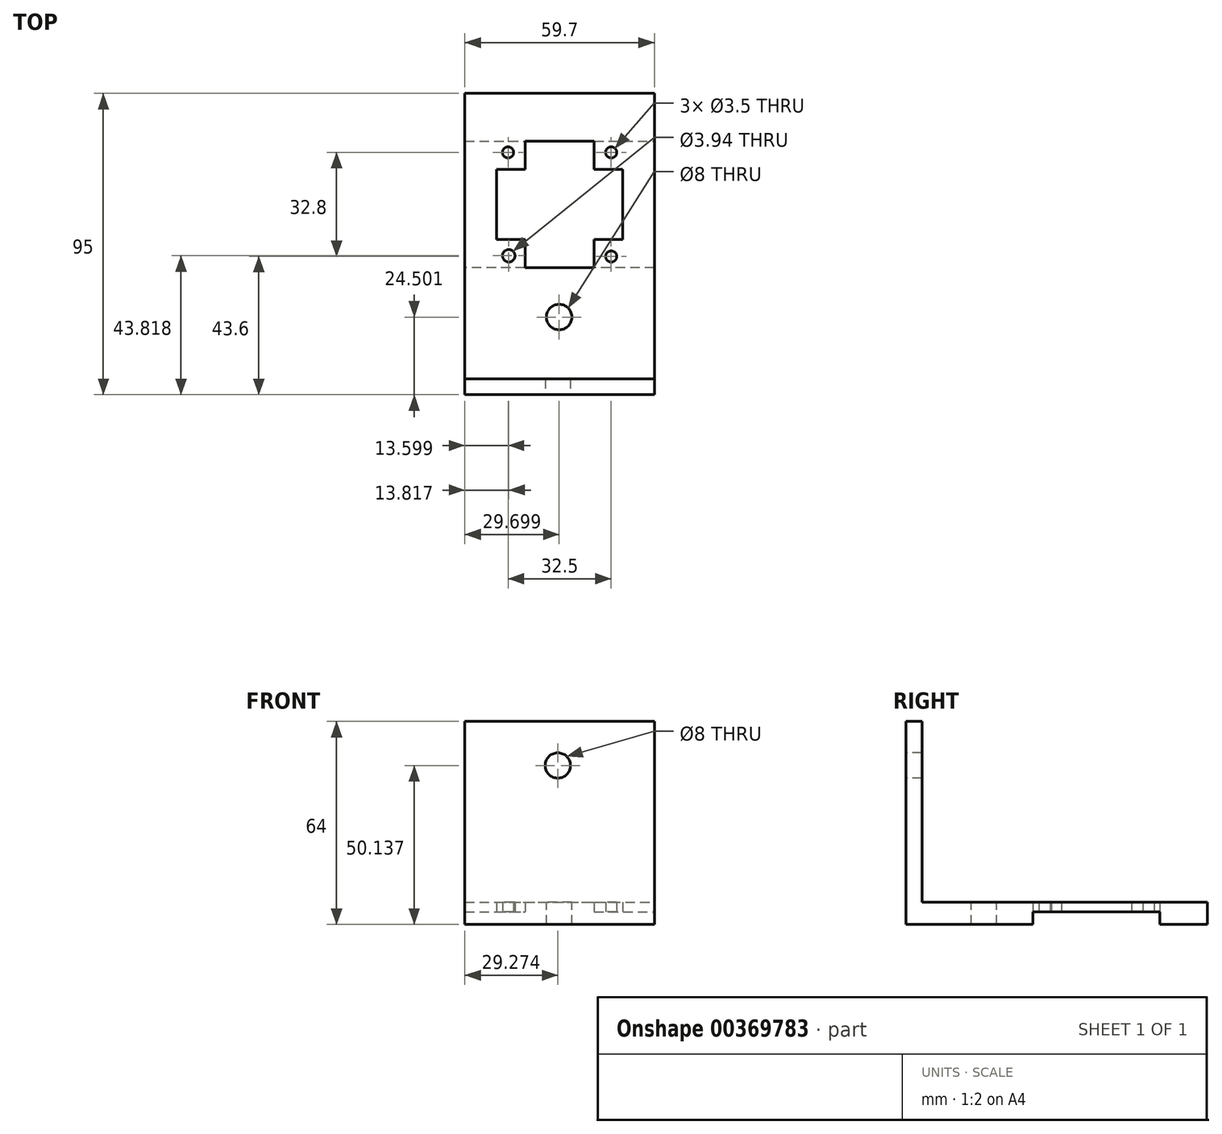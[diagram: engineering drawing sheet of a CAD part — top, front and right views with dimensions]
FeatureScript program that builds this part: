
annotation { "Feature Type Name" : "Feature", "Feature Type Description" : "" }
export const myFeature = defineFeature(function(context is Context, id is Id, definition is map)
    precondition{}
    {
        {
            var Q0;
            Q0=qCreatedBy(makeId("Top.planeOp"),FACE);
            var sketch = newSketch(context, id + "F0", { "sketchPlane" : qUnion([Q0])});
            skLineSegment(sketch, "E0.bottom", {"start": v(14.46, 0) * mm, "end": v(54.16, 0) * mm});
            skLineSegment(sketch, "E0.top", {"start": v(14.46, -40) * mm, "end": v(54.16, -40) * mm});
            skLineSegment(sketch, "E0.left", {"start": v(14.46, 0) * mm, "end": v(14.46, -40) * mm});
            skLineSegment(sketch, "E0.right", {"start": v(54.16, 0) * mm, "end": v(54.16, -40) * mm});
            skLineSegment(sketch, "E1", {"start": v(14.46, -9) * mm, "end": v(23.46, -9) * mm});
            skLineSegment(sketch, "E2", {"start": v(23.46, -9) * mm, "end": v(23.46, 0) * mm});
            skLineSegment(sketch, "E3", {"start": v(45.16, 0) * mm, "end": v(45.16, -9) * mm});
            skLineSegment(sketch, "E4", {"start": v(45.16, -9) * mm, "end": v(54.16, -9) * mm});
            skLineSegment(sketch, "E5", {"start": v(14.46, -31) * mm, "end": v(23.46, -31) * mm});
            skLineSegment(sketch, "E6", {"start": v(23.46, -31) * mm, "end": v(23.46, -40) * mm});
            skLineSegment(sketch, "E7", {"start": v(45.16, -40) * mm, "end": v(45.16, -31) * mm});
            skLineSegment(sketch, "E8", {"start": v(45.16, -31) * mm, "end": v(54.16, -31) * mm});
            skCircle(sketch, "E9", {"center": v(18.28, -36.18) * mm, "radius": 1.97 * mm});
            skCircle(sketch, "E10", {"center": v(18.06, -3.6) * mm, "radius": 1.75 * mm});
            skCircle(sketch, "E11", {"center": v(50.56, -3.6) * mm, "radius": 1.75 * mm});
            skCircle(sketch, "E12", {"center": v(50.56, -36.4) * mm, "radius": 1.75 * mm});
            skLineSegment(sketch, "E13", {"start": v(14.46, -40) * mm, "end": v(4.46, -40) * mm});
            skLineSegment(sketch, "E14", {"start": v(4.46, -40) * mm, "end": v(4.46, -50) * mm});
            skLineSegment(sketch, "E15", {"start": v(14.46, 0) * mm, "end": v(4.46, 0) * mm});
            skLineSegment(sketch, "E16", {"start": v(14.46, 0) * mm, "end": v(14.46, 10) * mm});
            skLineSegment(sketch, "E17", {"start": v(4.46, 0) * mm, "end": v(4.46, -40) * mm});
            skLineSegment(sketch, "E18", {"start": v(4.46, 0) * mm, "end": v(4.46, 10) * mm});
            skLineSegment(sketch, "E19", {"start": v(4.46, 10) * mm, "end": v(14.46, 10) * mm});
            skLineSegment(sketch, "E20", {"start": v(54.16, -40) * mm, "end": v(64.16, -40) * mm});
            skLineSegment(sketch, "E21", {"start": v(64.16, -40) * mm, "end": v(64.16, -50) * mm});
            skLineSegment(sketch, "E22", {"start": v(54.16, 0) * mm, "end": v(54.16, 10) * mm});
            skLineSegment(sketch, "E23", {"start": v(54.16, 0) * mm, "end": v(64.16, 0) * mm});
            skLineSegment(sketch, "E24", {"start": v(54.16, 10) * mm, "end": v(64.16, 10) * mm});
            skLineSegment(sketch, "E25", {"start": v(14.46, 10) * mm, "end": v(54.16, 10) * mm});
            skLineSegment(sketch, "E26", {"start": v(64.16, 10) * mm, "end": v(64.16, -40) * mm});
            skLineSegment(sketch, "E27", {"start": v(4.46, -50) * mm, "end": v(4.46, -80) * mm});
            skLineSegment(sketch, "E28", {"start": v(64.16, -50) * mm, "end": v(64.16, -80) * mm});
            skLineSegment(sketch, "E29", {"start": v(4.46, -80) * mm, "end": v(64.16, -80) * mm});
            skLineSegment(sketch, "E30", {"start": v(4.46, -75) * mm, "end": v(64.16, -75) * mm});
            skLineSegment(sketch, "E31", {"start": v(23.46, -40) * mm, "end": v(45.16, -40) * mm});
            skLineSegment(sketch, "E32", {"start": v(4.46, 10) * mm, "end": v(4.46, 15) * mm});
            skLineSegment(sketch, "E33", {"start": v(4.46, 15) * mm, "end": v(64.16, 15) * mm});
            skLineSegment(sketch, "E34", {"start": v(64.16, 10) * mm, "end": v(64.16, 15) * mm});
            skSolve(sketch);
        }
        {
            var Q0;
            Q0=makeQuery(id+"F0.imprint","IMPRINT",FACE,{"disambiguationData":[TD([[makeQuery(id+"F0.imprint","IMPRINT",EDGE,{"derivedFrom":sQuery(id+"F0.wireOp",EDGE,"E15")}),-1.0]])]});
            var Q1;
            Q1=makeQuery(id+"F0.imprint","IMPRINT",FACE,{"disambiguationData":[TD([[makeQuery(id+"F0.imprint","IMPRINT",EDGE,{"derivedFrom":sQuery(id+"F0.wireOp",EDGE,"E22")}),-1.0]])]});
            var Q2;
            {var subQ3=sQuery(id+"F0.wireOp",EDGE,"E16");Q2=makeQuery(id+"F0.imprint","IMPRINT",FACE,{"disambiguationData":[TD([[makeQuery(id+"F0.imprint","IMPRINT",EDGE,{"derivedFrom":subQ3}),-1.0]])]});}
            var Q3;
            {var subQ0=sQuery(id+"F0.wireOp",EDGE,"E13");Q3=makeQuery(id+"F0.imprint","IMPRINT",FACE,{"disambiguationData":[TD([[makeQuery(id+"F0.imprint","IMPRINT",EDGE,{"derivedFrom":subQ0}),-1.0]])]});}
            var Q4;
            {var subQ0=sQuery(id+"F0.wireOp",EDGE,"E20");Q4=makeQuery(id+"F0.imprint","IMPRINT",FACE,{"disambiguationData":[TD([[makeQuery(id+"F0.imprint","IMPRINT",EDGE,{"derivedFrom":subQ0}),1.0]])]});}
            var Q5;
            {var subQ4=sQuery(id+"F0.wireOp",EDGE,"E13");Q5=makeQuery(id+"F0.imprint","IMPRINT",FACE,{"disambiguationData":[TD([[makeQuery(id+"F0.imprint","IMPRINT",EDGE,{"derivedFrom":subQ4}),1.0]])]});}
            var Q6;
            {var subQ1=sQuery(id+"F0.wireOp",EDGE,"E1");Q6=makeQuery(id+"F0.imprint","IMPRINT",FACE,{"disambiguationData":[TD([[makeQuery(id+"F0.imprint","IMPRINT",EDGE,{"derivedFrom":subQ1}),1.0]])]});}
            var Q7;
            {var subQ1=sQuery(id+"F0.wireOp",EDGE,"E3");Q7=makeQuery(id+"F0.imprint","IMPRINT",FACE,{"disambiguationData":[TD([[makeQuery(id+"F0.imprint","IMPRINT",EDGE,{"derivedFrom":subQ1}),1.0]])]});}
            var Q8;
            {var subQ1=sQuery(id+"F0.wireOp",EDGE,"E5");Q8=makeQuery(id+"F0.imprint","IMPRINT",FACE,{"disambiguationData":[TD([[makeQuery(id+"F0.imprint","IMPRINT",EDGE,{"derivedFrom":subQ1}),-1.0]])]});}
            var Q9;
            {var subQ1=sQuery(id+"F0.wireOp",EDGE,"E7");Q9=makeQuery(id+"F0.imprint","IMPRINT",FACE,{"disambiguationData":[TD([[makeQuery(id+"F0.imprint","IMPRINT",EDGE,{"derivedFrom":subQ1}),-1.0]])]});}
            var Q10;
            Q10=makeQuery(id+"F0.imprint","IMPRINT",FACE,{"disambiguationData":[TD([[makeQuery(id+"F0.imprint","IMPRINT",EDGE,{"derivedFrom":sQuery(id+"F0.wireOp",EDGE,"E19")}),1.0]])]});
            extrude(context, id + "F1", {"entities" : qUnion([Q0, Q1, Q2, Q3, Q4, Q5, Q6, Q7, Q8, Q9, Q10]), "depth" : 3 * mm});
        }
        {
            var Q0;
            {var subQ0=sQuery(id+"F0.wireOp",EDGE,"E29");Q0=makeQuery(id+"F0.imprint","IMPRINT",FACE,{"disambiguationData":[TD([[makeQuery(id+"F0.imprint","IMPRINT",EDGE,{"derivedFrom":subQ0}),1.0]])]});}
            extrude(context, id + "F2", {"entities" : qUnion([Q0]), "operationType" : NewBodyOperationType.ADD, "depth" : 60 * mm});
        }
        {
            var Q0;
            Q0=makeQuery(id+"F2.opExtrude","SWEPT_FACE",FACE,{"disambiguationData":[OSD([sQuery(id+"F0.wireOp",EDGE,"E29")])]});
            var sketch = newSketch(context, id + "F3", { "sketchPlane" : qUnion([Q0])});
            skCircle(sketch, "E35", {"center": v(33.73, 46.14) * mm, "radius": 3.88 * mm});
            skSolve(sketch);
        }
        {
            var Q0;
            Q0=sQuery(id+"F3.wireOp",VERTEX,"E35.center");
            var Q1;
            Q1=makeQuery(id+"F1.opExtrude","SWEPT_BODY",BODY,{"disambiguationData":[OSD([sQuery(id+"F0.wireOp",EDGE,"E0.bottom"),sQuery(id+"F0.wireOp",EDGE,"E0.left"),sQuery(id+"F0.wireOp",EDGE,"E0.right"),sQuery(id+"F0.wireOp",EDGE,"E1"),sQuery(id+"F0.wireOp",EDGE,"E2"),sQuery(id+"F0.wireOp",EDGE,"E3"),sQuery(id+"F0.wireOp",EDGE,"E4"),sQuery(id+"F0.wireOp",EDGE,"E5"),sQuery(id+"F0.wireOp",EDGE,"E6"),sQuery(id+"F0.wireOp",EDGE,"E7"),sQuery(id+"F0.wireOp",EDGE,"E8"),sQuery(id+"F0.wireOp",EDGE,"E9"),sQuery(id+"F0.wireOp",EDGE,"E10"),sQuery(id+"F0.wireOp",EDGE,"E11"),sQuery(id+"F0.wireOp",EDGE,"E12"),sQuery(id+"F0.wireOp",EDGE,"E14"),sQuery(id+"F0.wireOp",EDGE,"E17"),sQuery(id+"F0.wireOp",EDGE,"E18"),sQuery(id+"F0.wireOp",EDGE,"E19"),sQuery(id+"F0.wireOp",EDGE,"E21"),sQuery(id+"F0.wireOp",EDGE,"E24"),sQuery(id+"F0.wireOp",EDGE,"E25"),sQuery(id+"F0.wireOp",EDGE,"E26"),sQuery(id+"F0.wireOp",EDGE,"E27"),sQuery(id+"F0.wireOp",EDGE,"E28"),sQuery(id+"F0.wireOp",EDGE,"E30"),sQuery(id+"F0.wireOp",EDGE,"E31")])]});
            hole(context, id + "F4", {"style" : HoleStyle.SIMPLE, "endStyle" : HoleEndStyle.THROUGH, "holeDiameter" : 8 * mm, "isTappedThrough" : true, "tappedDepth" : 12.7 * mm, "tapClearance" : 3, "locations" : qUnion([Q0]), "scope" : qUnion([Q1])});
        }
        {
            var Q0;
            {var subQ0=sQuery(id+"F0.wireOp",EDGE,"E30");var subQ1=sQuery(id+"F0.wireOp",EDGE,"E28");var subQ2=sQuery(id+"F0.wireOp",EDGE,"E27");Q0=makeQuery(id+"F2.boolean.opBoolean","MERGE",FACE,{"derivedFrom":[makeQuery(id+"F1.opExtrude","CAP_FACE",FACE,{"disambiguationData":[OSD([sQuery(id+"F0.wireOp",EDGE,"E0.bottom"),sQuery(id+"F0.wireOp",EDGE,"E0.left"),sQuery(id+"F0.wireOp",EDGE,"E0.right"),sQuery(id+"F0.wireOp",EDGE,"E1"),sQuery(id+"F0.wireOp",EDGE,"E2"),sQuery(id+"F0.wireOp",EDGE,"E3"),sQuery(id+"F0.wireOp",EDGE,"E4"),sQuery(id+"F0.wireOp",EDGE,"E5"),sQuery(id+"F0.wireOp",EDGE,"E6"),sQuery(id+"F0.wireOp",EDGE,"E7"),sQuery(id+"F0.wireOp",EDGE,"E8"),sQuery(id+"F0.wireOp",EDGE,"E9"),sQuery(id+"F0.wireOp",EDGE,"E10"),sQuery(id+"F0.wireOp",EDGE,"E11"),sQuery(id+"F0.wireOp",EDGE,"E12"),sQuery(id+"F0.wireOp",EDGE,"E14"),sQuery(id+"F0.wireOp",EDGE,"E17"),sQuery(id+"F0.wireOp",EDGE,"E18"),sQuery(id+"F0.wireOp",EDGE,"E19"),sQuery(id+"F0.wireOp",EDGE,"E21"),sQuery(id+"F0.wireOp",EDGE,"E24"),sQuery(id+"F0.wireOp",EDGE,"E25"),sQuery(id+"F0.wireOp",EDGE,"E26"),subQ2,subQ1,subQ0,sQuery(id+"F0.wireOp",EDGE,"E31")])],"isStart":true}),makeQuery(id+"F2.opExtrude","CAP_FACE",FACE,{"disambiguationData":[OSD([subQ2,subQ1,sQuery(id+"F0.wireOp",EDGE,"E29"),subQ0])],"isStart":true})]});}
            var sketch = newSketch(context, id + "F5", { "sketchPlane" : qUnion([Q0])});
            skLineSegment(sketch, "E36", {"start": v(23.46, 40) * mm, "end": v(4.46, 40) * mm});
            skLineSegment(sketch, "E37", {"start": v(45.16, 40) * mm, "end": v(64.16, 40) * mm});
            skLineSegment(sketch, "E38", {"start": v(64.16, 40) * mm, "end": v(64.16, 80) * mm});
            skLineSegment(sketch, "E39", {"start": v(64.16, 80) * mm, "end": v(4.46, 80) * mm});
            skLineSegment(sketch, "E40", {"start": v(4.46, 80) * mm, "end": v(4.46, 40) * mm});
            skLineSegment(sketch, "E41", {"start": v(4.46, -10) * mm, "end": v(4.46, -15) * mm});
            skLineSegment(sketch, "E42", {"start": v(64.16, -10) * mm, "end": v(64.16, -15) * mm});
            skLineSegment(sketch, "E43", {"start": v(4.46, -15) * mm, "end": v(64.16, -15) * mm});
            skLineSegment(sketch, "E44", {"start": v(23.46, 0) * mm, "end": v(4.46, 0) * mm});
            skLineSegment(sketch, "E45", {"start": v(4.46, 0) * mm, "end": v(4.46, -10) * mm});
            skLineSegment(sketch, "E46", {"start": v(45.16, 0) * mm, "end": v(64.16, 0) * mm});
            skLineSegment(sketch, "E47", {"start": v(64.16, 0) * mm, "end": v(64.16, -10) * mm});
            skSolve(sketch);
        }
        {
            var Q0;
            Q0 = qSketchRegion(id + "F5", true);
            var Q1;
            Q1=makeQuery(id+"F5.imprint","IMPRINT",FACE,{"disambiguationData":[TD([[makeQuery(id+"F5.imprint","IMPRINT",EDGE,{"derivedFrom":sQuery(id+"F5.wireOp",EDGE,"E36")}),-1.0]])]});
            var Q2;
            Q2=makeQuery(id+"F5.imprint","IMPRINT",FACE,{"disambiguationData":[TD([[makeQuery(id+"F5.imprint","IMPRINT",EDGE,{"derivedFrom":sQuery(id+"F5.wireOp",EDGE,"E44")}),1.0]])]});
            var Q3;
            Q3=makeQuery(id+"F5.imprint","IMPRINT",FACE,{"disambiguationData":[TD([[makeQuery(id+"F5.imprint","IMPRINT",EDGE,{"derivedFrom":sQuery(id+"F5.wireOp",EDGE,"E41")}),1.0]])]});
            extrude(context, id + "F6", {"entities" : qUnion([Q0, Q1, Q2, Q3]), "operationType" : NewBodyOperationType.ADD, "depth" : 4 * mm});
        }
        {
            var Q0;
            Q0=makeQuery(id+"F1.opExtrude","CAP_FACE",FACE,{"disambiguationData":[OSD([sQuery(id+"F0.wireOp",EDGE,"E0.bottom"),sQuery(id+"F0.wireOp",EDGE,"E0.left"),sQuery(id+"F0.wireOp",EDGE,"E0.right"),sQuery(id+"F0.wireOp",EDGE,"E1"),sQuery(id+"F0.wireOp",EDGE,"E2"),sQuery(id+"F0.wireOp",EDGE,"E3"),sQuery(id+"F0.wireOp",EDGE,"E4"),sQuery(id+"F0.wireOp",EDGE,"E5"),sQuery(id+"F0.wireOp",EDGE,"E6"),sQuery(id+"F0.wireOp",EDGE,"E7"),sQuery(id+"F0.wireOp",EDGE,"E8"),sQuery(id+"F0.wireOp",EDGE,"E9"),sQuery(id+"F0.wireOp",EDGE,"E10"),sQuery(id+"F0.wireOp",EDGE,"E11"),sQuery(id+"F0.wireOp",EDGE,"E12"),sQuery(id+"F0.wireOp",EDGE,"E14"),sQuery(id+"F0.wireOp",EDGE,"E17"),sQuery(id+"F0.wireOp",EDGE,"E18"),sQuery(id+"F0.wireOp",EDGE,"E21"),sQuery(id+"F0.wireOp",EDGE,"E26"),sQuery(id+"F0.wireOp",EDGE,"E27"),sQuery(id+"F0.wireOp",EDGE,"E28"),sQuery(id+"F0.wireOp",EDGE,"E30"),sQuery(id+"F0.wireOp",EDGE,"E31"),sQuery(id+"F0.wireOp",EDGE,"E32"),sQuery(id+"F0.wireOp",EDGE,"E33"),sQuery(id+"F0.wireOp",EDGE,"E34")])],"isStart":false});
            var sketch = newSketch(context, id + "F7", { "sketchPlane" : qUnion([Q0])});
            skCircle(sketch, "E48", {"center": v(34.16, -55.5) * mm, "radius": 3.5 * mm});
            skSolve(sketch);
        }
        {
            var Q0;
            Q0=sQuery(id+"F7.wireOp",VERTEX,"E48.center");
            var Q1;
            Q1=sQuery(id+"F7.wireOp",VERTEX,"iFjzwjUb-WjNj-5iLp-2EeU-WbCBWAUuZiUl.center");
            var Q2;
            Q2=makeQuery(id+"F1.opExtrude","SWEPT_BODY",BODY,{"disambiguationData":[OSD([sQuery(id+"F0.wireOp",EDGE,"E0.bottom"),sQuery(id+"F0.wireOp",EDGE,"E0.left"),sQuery(id+"F0.wireOp",EDGE,"E0.right"),sQuery(id+"F0.wireOp",EDGE,"E1"),sQuery(id+"F0.wireOp",EDGE,"E2"),sQuery(id+"F0.wireOp",EDGE,"E3"),sQuery(id+"F0.wireOp",EDGE,"E4"),sQuery(id+"F0.wireOp",EDGE,"E5"),sQuery(id+"F0.wireOp",EDGE,"E6"),sQuery(id+"F0.wireOp",EDGE,"E7"),sQuery(id+"F0.wireOp",EDGE,"E8"),sQuery(id+"F0.wireOp",EDGE,"E9"),sQuery(id+"F0.wireOp",EDGE,"E10"),sQuery(id+"F0.wireOp",EDGE,"E11"),sQuery(id+"F0.wireOp",EDGE,"E12"),sQuery(id+"F0.wireOp",EDGE,"E14"),sQuery(id+"F0.wireOp",EDGE,"E17"),sQuery(id+"F0.wireOp",EDGE,"E18"),sQuery(id+"F0.wireOp",EDGE,"E21"),sQuery(id+"F0.wireOp",EDGE,"E26"),sQuery(id+"F0.wireOp",EDGE,"E27"),sQuery(id+"F0.wireOp",EDGE,"E28"),sQuery(id+"F0.wireOp",EDGE,"E30"),sQuery(id+"F0.wireOp",EDGE,"E31"),sQuery(id+"F0.wireOp",EDGE,"E32"),sQuery(id+"F0.wireOp",EDGE,"E33"),sQuery(id+"F0.wireOp",EDGE,"E34")])]});
            hole(context, id + "F8", {"style" : HoleStyle.SIMPLE, "endStyle" : HoleEndStyle.THROUGH, "holeDiameter" : 8 * mm, "isTappedThrough" : true, "tappedDepth" : 12.7 * mm, "tapClearance" : 3, "locations" : qUnion([Q0, Q1]), "scope" : qUnion([Q2])});
        }
    });
